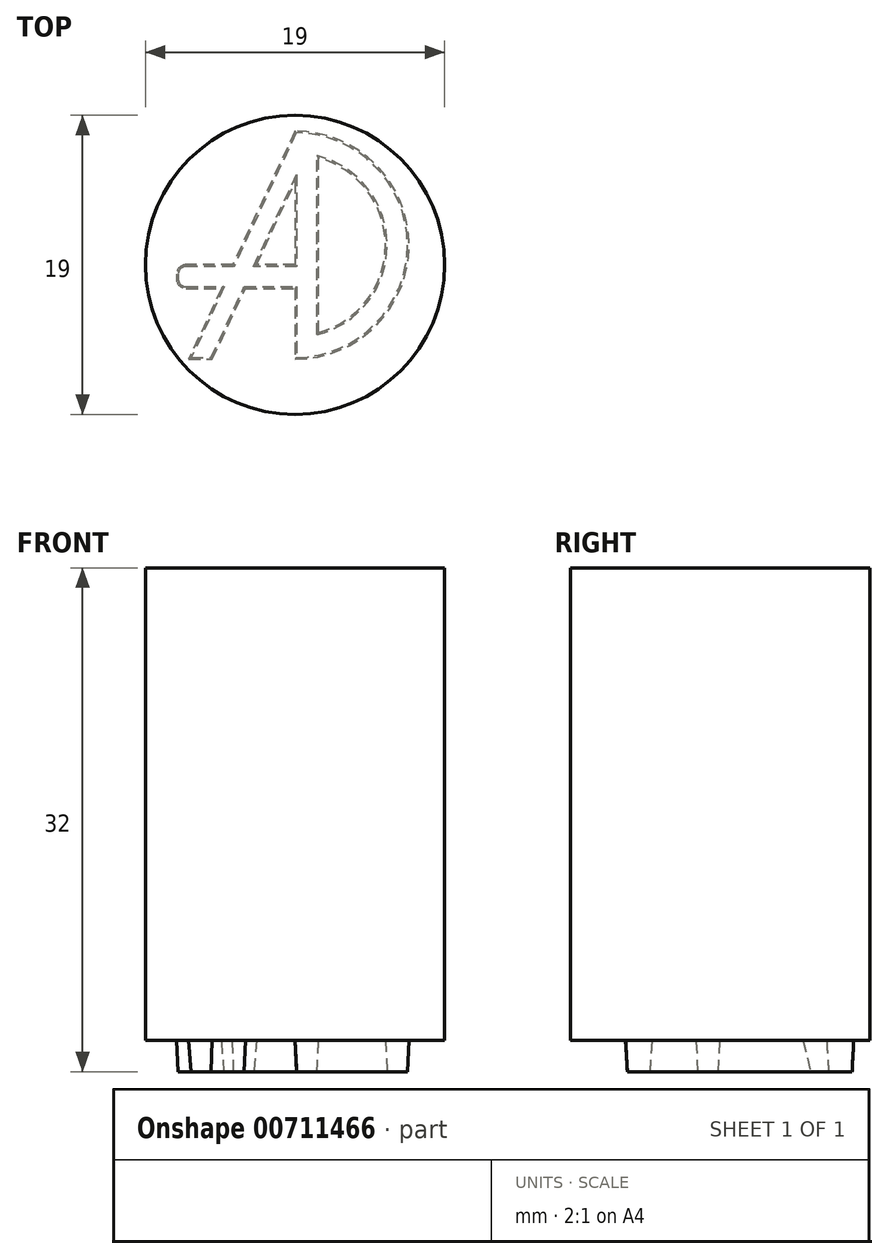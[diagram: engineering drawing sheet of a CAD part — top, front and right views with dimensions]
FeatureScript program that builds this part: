
annotation { "Feature Type Name" : "Feature", "Feature Type Description" : "" }
export const myFeature = defineFeature(function(context is Context, id is Id, definition is map)
    precondition{}
    {
        {
            var Q0;
            Q0=qCreatedBy(makeId("Top.planeOp"),FACE);
            var sketch = newSketch(context, id + "F0", { "sketchPlane" : qUnion([Q0])});
            skCircle(sketch, "E0", {"center": v(0, 0) * mm, "radius": 9.5 * mm});
            skLineSegment(sketch, "E1", {"start": v(0, 8.49) * mm, "end": v(-3.96, 0) * mm});
            skLineSegment(sketch, "E2", {"start": v(-6.76, -6) * mm, "end": v(-5.26, -6) * mm});
            skLineSegment(sketch, "E3", {"start": v(-5.26, -6) * mm, "end": v(-3.16, -1.5) * mm});
            skLineSegment(sketch, "E4", {"start": v(-3.16, -1.5) * mm, "end": v(0, -1.5) * mm});
            skLineSegment(sketch, "E5", {"start": v(0, -1.5) * mm, "end": v(0, -6) * mm});
            skLineSegment(sketch, "E6", {"start": v(-2.46, 0) * mm, "end": v(0, 5.27) * mm});
            skLineSegment(sketch, "E7", {"start": v(0, 0) * mm, "end": v(0, 5.27) * mm});
            skLineSegment(sketch, "E8", {"start": v(-2.46, 0) * mm, "end": v(0, 0) * mm});
            skLineSegment(sketch, "E9", {"start": v(-3.96, 0) * mm, "end": v(-6.92, 0) * mm});
            skLineSegment(sketch, "E10", {"start": v(-7.52, -0.6) * mm, "end": v(-7.52, -0.9) * mm});
            skLineSegment(sketch, "E11", {"start": v(-6.92, -1.5) * mm, "end": v(-4.66, -1.5) * mm});
            skLineSegment(sketch, "E12.trimOffspring", {"start": v(-4.66, -1.5) * mm, "end": v(-6.76, -6) * mm});
            skPoint(sketch, "E13.visualSharp", {"position": v(-7.52, 0) * mm});
            skArc(sketch, "E13.filletArc", {"start": v(-6.92, 0) * mm, "mid": v(-7.35, -0.18) * mm, "end": v(-7.52, -0.6) * mm});
            skPoint(sketch, "E14.visualSharp", {"position": v(-7.52, -1.5) * mm});
            skArc(sketch, "E14.filletArc", {"start": v(-7.52, -0.9) * mm, "mid": v(-7.35, -1.32) * mm, "end": v(-6.92, -1.5) * mm});
            skArc(sketch, "E15", {"start": v(0, -6) * mm, "mid": v(7.24, 1.24) * mm, "end": v(0, 8.49) * mm});
            skLineSegment(sketch, "E16", {"start": v(0, 8.49) * mm, "end": v(0, -6) * mm, "construction": true});
            skLineSegment(sketch, "E17.0", {"start": v(1.5, 6.79) * mm, "end": v(1.5, -4.3) * mm});
            skArc(sketch, "E17.1", {"start": v(1.5, -4.3) * mm, "mid": v(5.74, 1.24) * mm, "end": v(1.5, 6.79) * mm});
            skLineSegment(sketch, "E18", {"start": v(1.5, 6.79) * mm, "end": v(1.5, -4.3) * mm, "construction": true});
            skSolve(sketch);
        }
        {
            var Q0;
            Q0=makeQuery(id+"F0.imprint","IMPRINT",FACE,{"disambiguationData":[TD([[makeQuery(id+"F0.imprint","IMPRINT",EDGE,{"derivedFrom":sQuery(id+"F0.wireOp",EDGE,"E1")}),1.0]])]});
            extrude(context, id + "F1", {"entities" : qUnion([Q0]), "oppositeDirection" : true, "depth" : 2 * mm, "offsetDistance" : 25 * mm, "hasDraft" : true, "draftAngle" : 3 * degree, "draftPullDirection" : true});
        }
        {
            var Q0;
            Q0=makeQuery(id+"F0.imprint","IMPRINT",FACE,{"disambiguationData":[TD([[makeQuery(id+"F0.imprint","IMPRINT",EDGE,{"derivedFrom":sQuery(id+"F0.wireOp",EDGE,"E0")}),1.0]])]});
            var Q1;
            Q1=makeQuery(id+"F0.imprint","IMPRINT",FACE,{"disambiguationData":[TD([[makeQuery(id+"F0.imprint","IMPRINT",EDGE,{"derivedFrom":sQuery(id+"F0.wireOp",EDGE,"E1")}),1.0]])]});
            var Q2;
            Q2=makeQuery(id+"F0.imprint","IMPRINT",FACE,{"disambiguationData":[TD([[makeQuery(id+"F0.imprint","IMPRINT",EDGE,{"derivedFrom":sQuery(id+"F0.wireOp",EDGE,"E6")}),-1.0]])]});
            var Q3;
            Q3=makeQuery(id+"F0.imprint","IMPRINT",FACE,{"disambiguationData":[TD([[makeQuery(id+"F0.imprint","IMPRINT",EDGE,{"derivedFrom":sQuery(id+"F0.wireOp",EDGE,"E17.0")}),1.0]])]});
            extrude(context, id + "F2", {"entities" : qUnion([Q0, Q1, Q2, Q3]), "depth" : 30 * mm, "offsetDistance" : 25 * mm});
        }
    });
